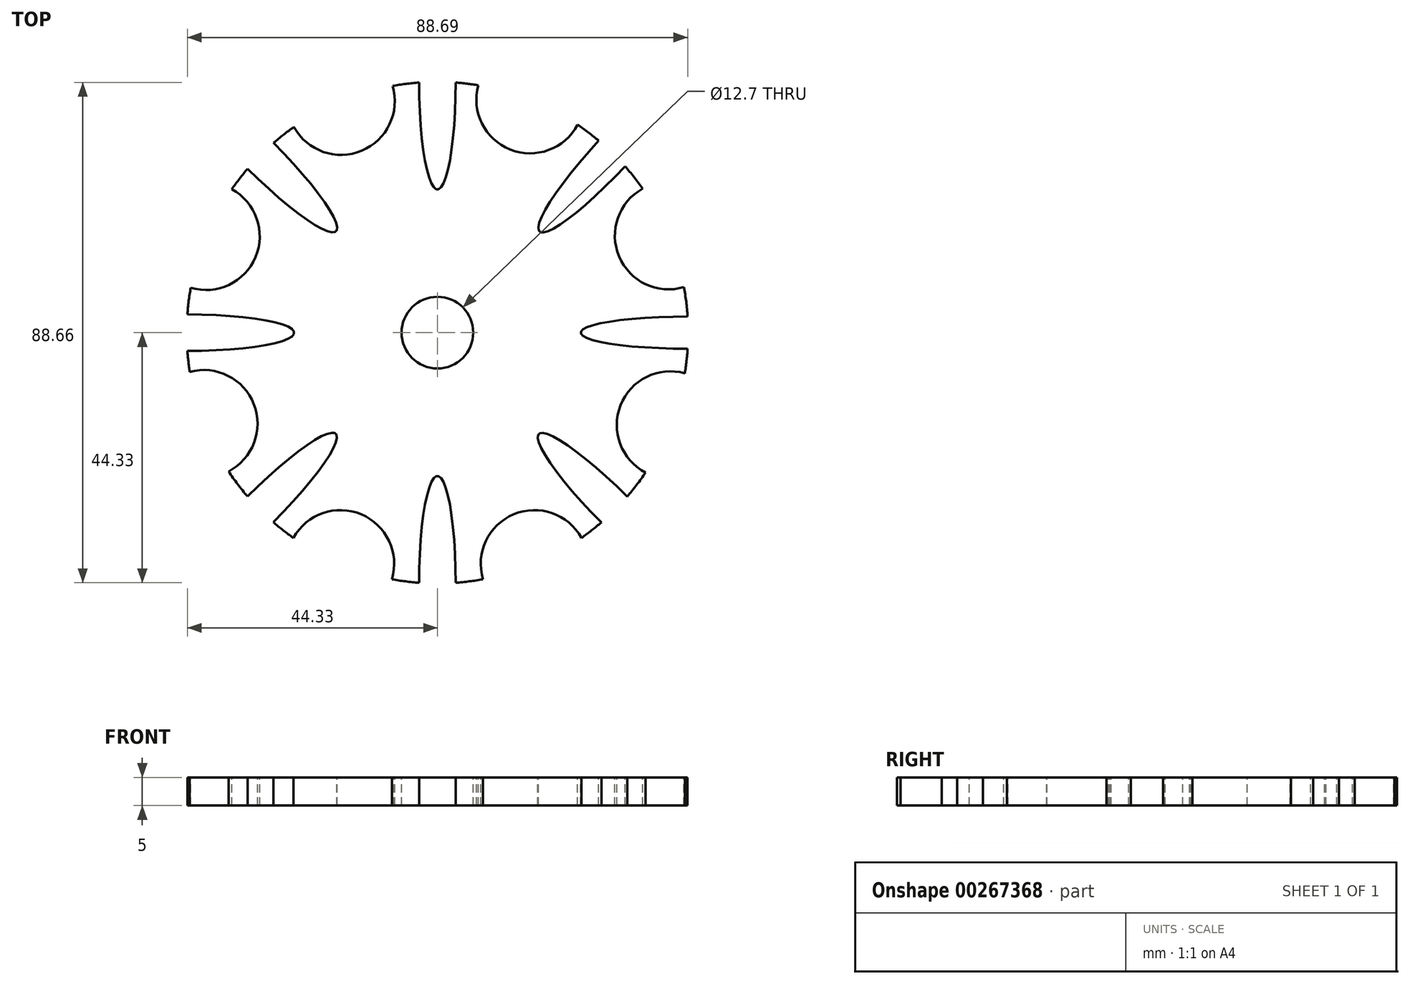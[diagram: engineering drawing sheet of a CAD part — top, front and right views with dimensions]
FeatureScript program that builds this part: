
annotation { "Feature Type Name" : "Feature", "Feature Type Description" : "" }
export const myFeature = defineFeature(function(context is Context, id is Id, definition is map)
    precondition{}
    {
        {
            var Q0;
            Q0=qCreatedBy(makeId("Top.planeOp"),FACE);
            var sketch = newSketch(context, id + "F0", { "sketchPlane" : qUnion([Q0])});
            skCircle(sketch, "E0", {"center": v(0, 0) * mm, "radius": 44.45 * mm});
            skEllipticalArc(sketch, "E1", {});
            skEllipticalArc(sketch, "E2", {});
            skEllipticalArc(sketch, "E3", {});
            skLineSegment(sketch, "E4", {"start": v(0, 0) * mm, "end": v(-31.43, 31.43) * mm});
            skLineSegment(sketch, "E5", {"start": v(0, 0) * mm, "end": v(31.43, -31.43) * mm});
            skLineSegment(sketch, "E6", {"start": v(0, 0) * mm, "end": v(31.43, 31.43) * mm});
            skLineSegment(sketch, "E7", {"start": v(0, 0) * mm, "end": v(-31.43, -31.43) * mm});
            skEllipticalArc(sketch, "E8", {});
            skEllipticalArc(sketch, "E9", {});
            skPoint(sketch, "E10.center.orphan", {"position": v(44.45, 0) * mm});
            skEllipticalArc(sketch, "E11", {});
            skEllipticalArc(sketch, "E12", {});
            skEllipticalArc(sketch, "E13", {});
            skArc(sketch, "E14", {"start": v(-37.02, -24.6) * mm, "mid": v(-32.54, -12.69) * mm, "end": v(-43.9, -6.95) * mm});
            skArc(sketch, "E15", {"start": v(-43.73, 7.95) * mm, "mid": v(-32.24, 13.42) * mm, "end": v(-36.45, 25.44) * mm});
            skArc(sketch, "E16", {"start": v(-25.44, 36.45) * mm, "mid": v(-13.42, 32.24) * mm, "end": v(-7.95, 43.73) * mm});
            skArc(sketch, "E17", {"start": v(7.24, 43.86) * mm, "mid": v(12.9, 32.45) * mm, "end": v(24.85, 36.86) * mm});
            skArc(sketch, "E18", {"start": v(36.38, 25.54) * mm, "mid": v(32.2, 13.51) * mm, "end": v(43.71, 8.07) * mm});
            skArc(sketch, "E19", {"start": v(43.86, -7.2) * mm, "mid": v(32.47, -12.87) * mm, "end": v(36.89, -24.8) * mm});
            skArc(sketch, "E20", {"start": v(-8.07, -43.71) * mm, "mid": v(-13.51, -32.2) * mm, "end": v(-25.54, -36.38) * mm});
            skArc(sketch, "E21", {"start": v(25.54, -36.38) * mm, "mid": v(13.51, -32.2) * mm, "end": v(8.07, -43.71) * mm});
            skCircle(sketch, "E22", {"center": v(0, 0) * mm, "radius": 6.35 * mm});
            const initialGuessF0  = {"E1": [0, 0.04445, 0, 1, 0.01905, 0.0032385000000000005, 1.5769972249809543, 4.706188082198632], "E2": [0, -0.04445, 0, 1, 0.01905, 0.0032385000000000005, 4.718589878570747, 1.564595428608839], "E3": [-0.04445, 0, -1, 0, 0.01905, 0.0032385000000000005, 1.5769972249809543, 4.706188082198632], "E8": [-0.03143089642374204, 0.03143089642374204, 0.7070813096325755, -0.7071322518230108, 0.01905, 0.0032385, 4.718596018093433, 1.564601568107963], "E9": [0.03143089642374204, -0.03143089642374204, -0.7071421696074867, 0.7070713909944432, 0.01905, 0.0032385000000000005, 4.718581348413236, 1.5645868984058442], "E11": [0.04445, 0, -1, 0, 0.01905, 0.0028575000000000002, 4.717215306796129, 1.5659700003834556], "E12": [-0.031477229278026174, -0.03139081617185074, -0.7071067811865476, -0.7071067811865475, 0.01905, 0.0032385000000000005, 1.5769972249809543, 4.706188082198632], "E13": [0.031062211365828547, 0.03190597939223769, 0.6798854098087299, 0.7333183684657133, 0.01905, 0.0032385000000000005, 1.5769972249809543, 4.706188082198632]};
            skSetInitialGuess(sketch, initialGuessF0);
            skSolve(sketch);
        }
        {
            var Q0;
            {var subQ5=sQuery(id+"F0.wireOp",EDGE,"E2");Q0=makeQuery(id+"F0.imprint","IMPRINT",FACE,{"disambiguationData":[TD([[makeQuery(id+"F0.imprint","IMPRINT",EDGE,{"derivedFrom":subQ5}),-1.0]])]});}
            var Q1;
            {var subQ7=sQuery(id+"F0.wireOp",EDGE,"E11");Q1=makeQuery(id+"F0.imprint","IMPRINT",FACE,{"disambiguationData":[TD([[makeQuery(id+"F0.imprint","IMPRINT",EDGE,{"derivedFrom":subQ7}),-1.0]])]});}
            var Q2;
            {var subQ0=sQuery(id+"F0.wireOp",EDGE,"E1");Q2=makeQuery(id+"F0.imprint","IMPRINT",FACE,{"disambiguationData":[TD([[makeQuery(id+"F0.imprint","IMPRINT",EDGE,{"derivedFrom":subQ0}),-1.0]])]});}
            var Q3;
            {var subQ5=sQuery(id+"F0.wireOp",EDGE,"E3");Q3=makeQuery(id+"F0.imprint","IMPRINT",FACE,{"disambiguationData":[TD([[makeQuery(id+"F0.imprint","IMPRINT",EDGE,{"derivedFrom":subQ5}),-1.0]])]});}
            extrude(context, id + "F1", {"entities" : qUnion([Q0, Q1, Q2, Q3]), "oppositeDirection" : true, "depth" : 5 * mm});
        }
    });
